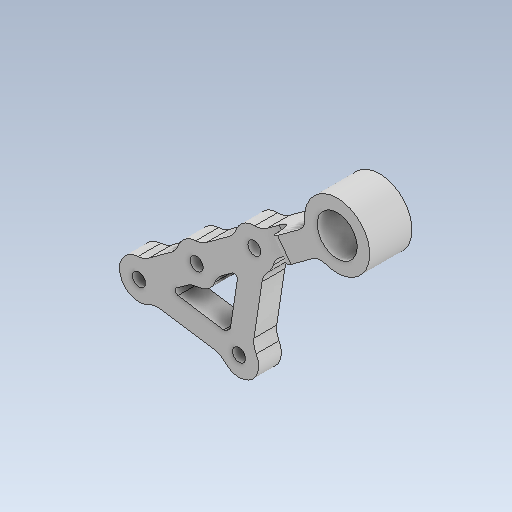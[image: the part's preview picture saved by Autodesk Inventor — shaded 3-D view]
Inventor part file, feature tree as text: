
AUTODESK INVENTOR PART (.ipt)
format: ipt  version: 2023 (Build 270158000, 158)  size: 247,808 bytes
history: native  units: mm
features: sketch x8, other x3, plane x1
ambient origin geometry x8: Origin, YZ Plane, XZ Plane, XY Plane, X Axis, Y Axis, Z Axis, Center Point
bodies: Solid1 (feature_tree)
feature tree (12):
  other  "leg_link_4.ipt"
  other  "Solid1::leg_link_4.ipt"
  other  "TaggingFeature1"
  sketch  "Sketch1"  dims[d0=10.0mm]
  sketch  "Sketch2"
  sketch  "Sketch3"
  sketch  "Sketch4"
  sketch  "Sketch5"
  sketch  "Sketch6"
  sketch  "Sketch7"
  sketch  "Sketch8"
  plane  "Work Plane1"
